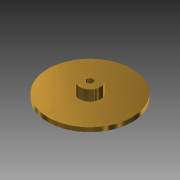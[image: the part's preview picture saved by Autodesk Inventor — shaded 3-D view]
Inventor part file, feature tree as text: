
AUTODESK INVENTOR PART (.ipt)
format: ipt  version: 2015 (Build 190159000, 159)  size: 116,736 bytes
history: native  units: mm
features: extrude x4, sketch x4
ambient origin geometry x8: Origin, YZ Plane, XZ Plane, XY Plane, X Axis, Y Axis, Z Axis, Center Point
bodies: Body1 (feature_tree)
feature tree (8):
  extrude  "押し出し3"  Depth=40.0mm
  extrude  "押し出し4"  Depth=2.0mm TaperAngle=0.0deg
  extrude  "押し出し5"  Depth=10.0mm
  extrude  "押し出し6"  Depth=5.0mm TaperAngle=0.0deg
  sketch  "スケッチ4"
  sketch  "スケッチ5"
  sketch  "スケッチ6"
  sketch  "スケッチ7"
